# Revit family: НЕВАТОМ_Шибер-D_20220407
name_source: partatom
category: Арматура воздуховодов
revit_build: Autodesk Revit 2017 (Build: 20170118_1100(x64)
units: mm (PartAtom-declared; Revit-internal decimal feet)

## family parameters
Всегда вертикально = Нет
На основе рабочей плоскости = Нет
Общий = Нет
При загрузке вырезать с полостями = Нет
Размер круглого соединителя = Использовать диаметр
Тип детали = Вставляется

## types (15) — shared parameters
150 = 150 мм
20 = 20 мм
ADSK_Единица измерения = шт.
ADSK_Завод-изготовитель = NEVATOM
ADSK_Масса_Текст = кг
ADSK_Материал наименование = Оцинкованная сталь
ADSK_Наименование = Шибер
ADSK_Напряжение = 0 В
ADSK_Полная мощность = 0 В·А
ADSK_Потеря давления воздуха = 0.0 Па
ADSK_Размер_Ширина = 150 мм
ADSK_Расход воздуха = 0.0 л/с
ADSK_Ток = 0 А
L = 15 мм
Nevatom_URL = https://t.me
t = 1 мм
Материал корпуса = Материал корпуса
zero-valued in all types: ADSK_Масса

## per-type parameters (varying)
| type | A | ADSK_Марка | ADSK_Размер_Высота | ADSK_Размер_Длина | B | D | D+5 | Dt |
| 100 | 155 мм | 100–ОЦ.–0,7–T2.T2 | 155 мм | 275 мм | 275 мм | 100 мм | 65 мм | 102 мм |
| 125 | 180 мм | 125–ОЦ.–0,7–T2.T2 | 180 мм | 320 мм | 320 мм | 125 мм | 78 мм | 127 мм |
| 160 | 225 мм | 160–ОЦ.–0,7–T2.T2 | 225 мм | 405 мм | 405 мм | 160 мм | 95 мм | 162 мм |
| 200 | 265 мм | 200–ОЦ.–0,7–T2.T2 | 265 мм | 485 мм | 485 мм | 200 мм | 115 мм | 202 мм |
| 250 | 315 мм | 250–ОЦ.–0,7–T2.T2 | 315 мм | 585 мм | 585 мм | 250 мм | 140 мм | 252 мм |
| 280 | 345 мм | 280–ОЦ.–0,7–T2.T2 | 345 мм | 615 мм | 615 мм | 280 мм | 155 мм | 282 мм |
| 315 | 380 мм | 315–ОЦ.–0,7–T2.T2 | 380 мм | 715 мм | 715 мм | 315 мм | 173 мм | 317 мм |
| 355 | 420 мм | 355–ОЦ.–0,7–T2.T2 | 420 мм | 795 мм | 795 мм | 355 мм | 193 мм | 357 мм |
| 400 | 465 мм | 400–ОЦ.–0,7–T2.T2 | 465 мм | 885 мм | 885 мм | 400 мм | 215 мм | 402 мм |
| 450 | 515 мм | 450–ОЦ.–0,7–T2.T2 | 515 мм | 1005 мм | 1005 мм | 450 мм | 240 мм | 452 мм |
| 500 | 565 мм | 500–ОЦ.–0,7–T2.T2 | 565 мм | 1085 мм | 1085 мм | 500 мм | 265 мм | 502 мм |
| 560 | 625 мм | 560–ОЦ.–0,7–T2.T2 | 625 мм | 1205 мм | 1205 мм | 560 мм | 295 мм | 562 мм |
| 630 | 695 мм | 630–ОЦ.–0,7–T2.T2 | 695 мм | 1365 мм | 1365 мм | 630 мм | 330 мм | 632 мм |
| 710 | 782 мм | 710–ОЦ.–0,7–T2.T2 | 782 мм | 1505 мм | 1505 мм | 710 мм | 370 мм | 712 мм |
| 800 | 885 мм | 800–ОЦ.–0,7–T2.T2 | 885 мм | 1685 мм | 1685 мм | 800 мм | 415 мм | 802 мм |
